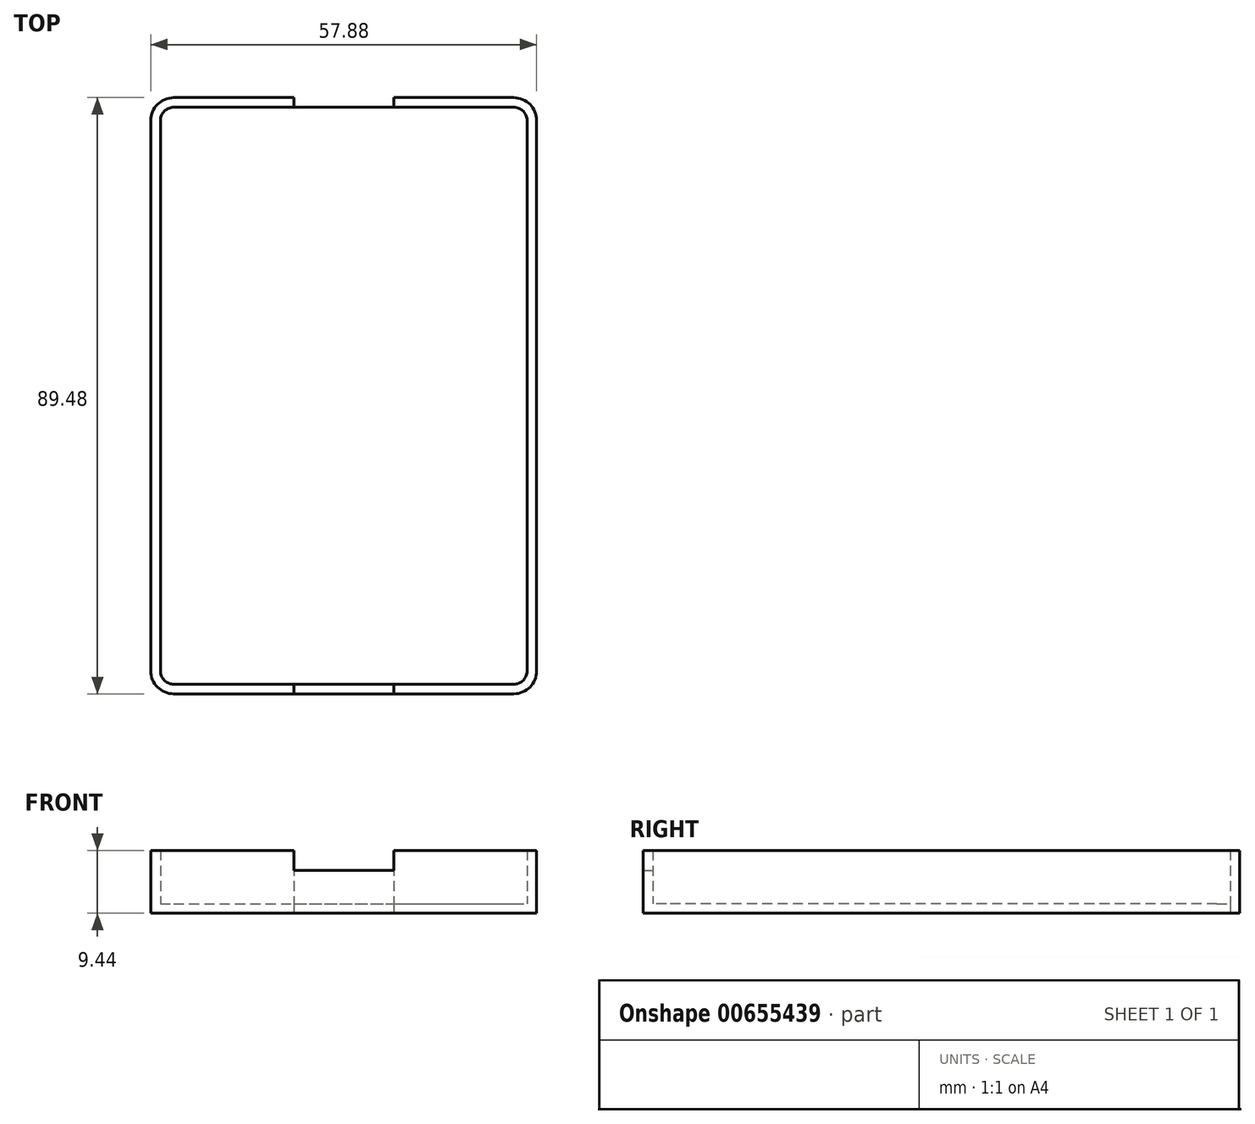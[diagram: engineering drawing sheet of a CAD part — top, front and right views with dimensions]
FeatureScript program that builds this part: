
annotation { "Feature Type Name" : "Feature", "Feature Type Description" : "" }
export const myFeature = defineFeature(function(context is Context, id is Id, definition is map)
    precondition{}
    {
        {
            var Q0;
            Q0=qCreatedBy(makeId("Top.planeOp"),FACE);
            var sketch = newSketch(context, id + "F0", { "sketchPlane" : qUnion([Q0])});
            skLineSegment(sketch, "E0.bottom", {"start": v(-27.5, 43.3) * mm, "end": v(27.5, 43.3) * mm});
            skLineSegment(sketch, "E0.top", {"start": v(-27.5, -43.3) * mm, "end": v(27.5, -43.3) * mm});
            skLineSegment(sketch, "E0.left", {"start": v(-27.5, 43.3) * mm, "end": v(-27.5, -43.3) * mm});
            skLineSegment(sketch, "E0.right", {"start": v(27.5, 43.3) * mm, "end": v(27.5, -43.3) * mm});
            skPoint(sketch, "E0.middle", {"position": v(0, 0) * mm});
            skSolve(sketch);
        }
        {
            var Q0;
            Q0=makeQuery(id+"F0.imprint","IMPRINT",FACE,{"disambiguationData":[TD([[makeQuery(id+"F0.imprint","IMPRINT",EDGE,{"derivedFrom":sQuery(id+"F0.wireOp",EDGE,"E0.bottom")}),-1.0]])]});
            extrude(context, id + "F1", {"entities" : qUnion([Q0]), "depth" : 8 * mm, "offsetDistance" : 25 * mm});
        }
        {
            var Q0;
            Q0=makeQuery(id+"F1.opExtrude","SWEPT_EDGE",EDGE,{"disambiguationData":[OSD([sQuery(id+"F0.wireOp",EDGE,"E0.top"),sQuery(id+"F0.wireOp",EDGE,"E0.left")])]});
            var Q1;
            Q1=makeQuery(id+"F1.opExtrude","SWEPT_EDGE",EDGE,{"disambiguationData":[OSD([sQuery(id+"F0.wireOp",EDGE,"E0.top"),sQuery(id+"F0.wireOp",EDGE,"E0.right")])]});
            var Q2;
            Q2=makeQuery(id+"F1.opExtrude","SWEPT_EDGE",EDGE,{"disambiguationData":[OSD([sQuery(id+"F0.wireOp",EDGE,"E0.bottom"),sQuery(id+"F0.wireOp",EDGE,"E0.right")])]});
            var Q3;
            Q3=makeQuery(id+"F1.opExtrude","SWEPT_EDGE",EDGE,{"disambiguationData":[OSD([sQuery(id+"F0.wireOp",EDGE,"E0.bottom"),sQuery(id+"F0.wireOp",EDGE,"E0.left")])]});
            fillet(context, id + "F2", {"entities" : qUnion([Q0, Q1, Q2, Q3]), "radius" : 2 * mm, "tangentPropagation" : true, "allowEdgeOverflow" : false});
        }
        {
            var Q0;
            Q0=makeQuery(id+"F1.opExtrude","CAP_FACE",FACE,{"disambiguationData":[OSD([sQuery(id+"F0.wireOp",EDGE,"E0.bottom"),sQuery(id+"F0.wireOp",EDGE,"E0.top"),sQuery(id+"F0.wireOp",EDGE,"E0.left"),sQuery(id+"F0.wireOp",EDGE,"E0.right")])],"isStart":false});
            shell(context, id + "F3", {"entities" : qUnion([Q0]), "thickness" : (0.48 * 3) * mm, "oppositeDirection" : true});
        }
        {
            var Q0;
            Q0=qCreatedBy(makeId("Front.planeOp"),FACE);
            var sketch = newSketch(context, id + "F4", { "sketchPlane" : qUnion([Q0])});
            skLineSegment(sketch, "E1.0.0", {"start": v(25.5, 8) * mm, "end": v(-25.5, 8) * mm, "construction": true});
            skLineSegment(sketch, "E1.0.1", {"start": v(-25.5, 8) * mm, "end": v(-25.5, -1.44) * mm, "construction": true});
            skLineSegment(sketch, "E1.0.2", {"start": v(-25.5, -1.44) * mm, "end": v(25.5, -1.44) * mm, "construction": true});
            skLineSegment(sketch, "E1.0.3", {"start": v(25.5, -1.44) * mm, "end": v(25.5, 8) * mm, "construction": true});
            skLineSegment(sketch, "E2.bottom", {"start": v(-7.5, 8) * mm, "end": v(7.5, 8) * mm});
            skLineSegment(sketch, "E2.top", {"start": v(-7.5, 5) * mm, "end": v(7.5, 5) * mm});
            skLineSegment(sketch, "E2.left", {"start": v(-7.5, 8) * mm, "end": v(-7.5, 5) * mm});
            skLineSegment(sketch, "E2.right", {"start": v(7.5, 8) * mm, "end": v(7.5, 5) * mm});
            skLineSegment(sketch, "E3", {"start": v(0, 0) * mm, "end": v(0, 8) * mm, "construction": true});
            skSolve(sketch);
        }
        {
            var Q0;
            Q0 = qSketchRegion(id + "F4", true);
            extrude(context, id + "F5", {"entities" : qUnion([Q0]), "operationType" : NewBodyOperationType.REMOVE, "endBound" : BoundingType.SYMMETRIC, "depth" : 96.2 * mm, "offsetDistance" : 25 * mm});
        }
        {
            var Q0;
            Q0=makeQuery(id+"F1.opExtrude","CAP_FACE",FACE,{"disambiguationData":[OSD([sQuery(id+"F0.wireOp",EDGE,"E0.bottom"),sQuery(id+"F0.wireOp",EDGE,"E0.top"),sQuery(id+"F0.wireOp",EDGE,"E0.left"),sQuery(id+"F0.wireOp",EDGE,"E0.right")])],"isStart":true});
            var sketch = newSketch(context, id + "F6", { "sketchPlane" : qUnion([Q0])});
            skPoint(sketch, "E4.0", {"position": v(-7.5, -44.74) * mm});
            skPoint(sketch, "E5.0", {"position": v(7.5, -44.74) * mm});
            skPoint(sketch, "E6.0", {"position": v(-7.5, -43.3) * mm});
            skLineSegment(sketch, "E7.bottom", {"start": v(7.5, -44.74) * mm, "end": v(-7.5, -44.74) * mm});
            skLineSegment(sketch, "E7.top", {"start": v(7.5, -43.3) * mm, "end": v(-7.5, -43.3) * mm});
            skLineSegment(sketch, "E7.left", {"start": v(7.5, -44.74) * mm, "end": v(7.5, -43.3) * mm});
            skLineSegment(sketch, "E7.right", {"start": v(-7.5, -44.74) * mm, "end": v(-7.5, -43.3) * mm});
            skSolve(sketch);
        }
        {
            var Q0;
            Q0 = qSketchRegion(id + "F6", true);
            extrude(context, id + "F7", {"entities" : qUnion([Q0]), "operationType" : NewBodyOperationType.REMOVE, "oppositeDirection" : true, "depth" : 25 * mm, "offsetDistance" : 25 * mm});
        }
    });
